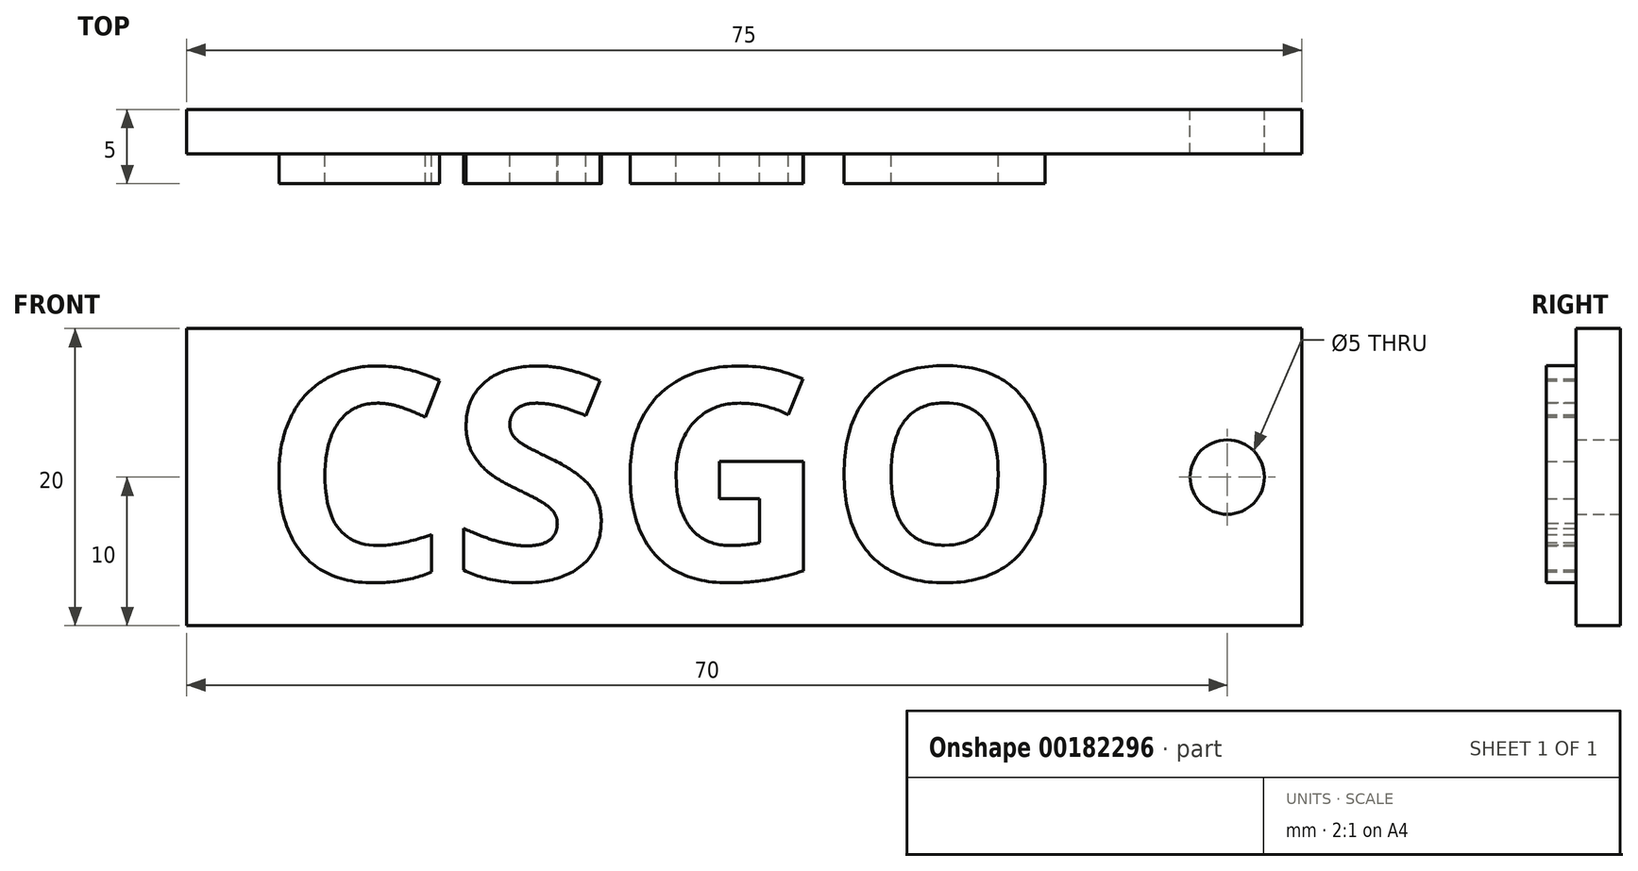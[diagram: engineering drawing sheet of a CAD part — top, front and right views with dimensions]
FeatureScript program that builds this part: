
annotation { "Feature Type Name" : "Feature", "Feature Type Description" : "" }
export const myFeature = defineFeature(function(context is Context, id is Id, definition is map)
    precondition{}
    {
        {
            var Q0;
            Q0=qCreatedBy(makeId("Front.planeOp"),FACE);
            var sketch = newSketch(context, id + "F0", { "sketchPlane" : qUnion([Q0])});
            skLineSegment(sketch, "E0.bottom", {"start": v(0, 0) * mm, "end": v(75, 0) * mm});
            skLineSegment(sketch, "E0.top", {"start": v(0, -20) * mm, "end": v(75, -20) * mm});
            skLineSegment(sketch, "E0.left", {"start": v(0, 0) * mm, "end": v(0, -20) * mm});
            skLineSegment(sketch, "E0.right", {"start": v(75, 0) * mm, "end": v(75, -20) * mm});
            skCircle(sketch, "E1", {"center": v(70, -10) * mm, "radius": 2.5 * mm});
            skSolve(sketch);
        }
        {
            var Q0;
            Q0 = qSketchRegion(id + "F0", true);
            extrude(context, id + "F1", {"entities" : qUnion([Q0]), "depth" : 3 * mm});
        }
        {
            var Q0;
            Q0=makeQuery(id+"F1.opExtrude","CAP_FACE",FACE,{"disambiguationData":[OSD([sQuery(id+"F0.wireOp",EDGE,"E0.bottom"),sQuery(id+"F0.wireOp",EDGE,"E0.top"),sQuery(id+"F0.wireOp",EDGE,"E0.left"),sQuery(id+"F0.wireOp",EDGE,"E0.right"),sQuery(id+"F0.wireOp",EDGE,"E1")])],"isStart":false});
            var sketch = newSketch(context, id + "F2", { "sketchPlane" : qUnion([Q0])});
            skText(sketch, "E2", { "text": "CSGO", "fontName": "OpenSans-Bold.ttf"});
            const initialGuessF2  = {"E2": [0.00504, -0.01692, 1, 0, 0.01432]};
            skSetInitialGuess(sketch, initialGuessF2);
            skSolve(sketch);
        }
        {
            var Q0;
            Q0 = qSketchRegion(id + "F2", true);
            extrude(context, id + "F3", {"entities" : qUnion([Q0]), "operationType" : NewBodyOperationType.ADD, "depth" : 2 * mm});
        }
    });
